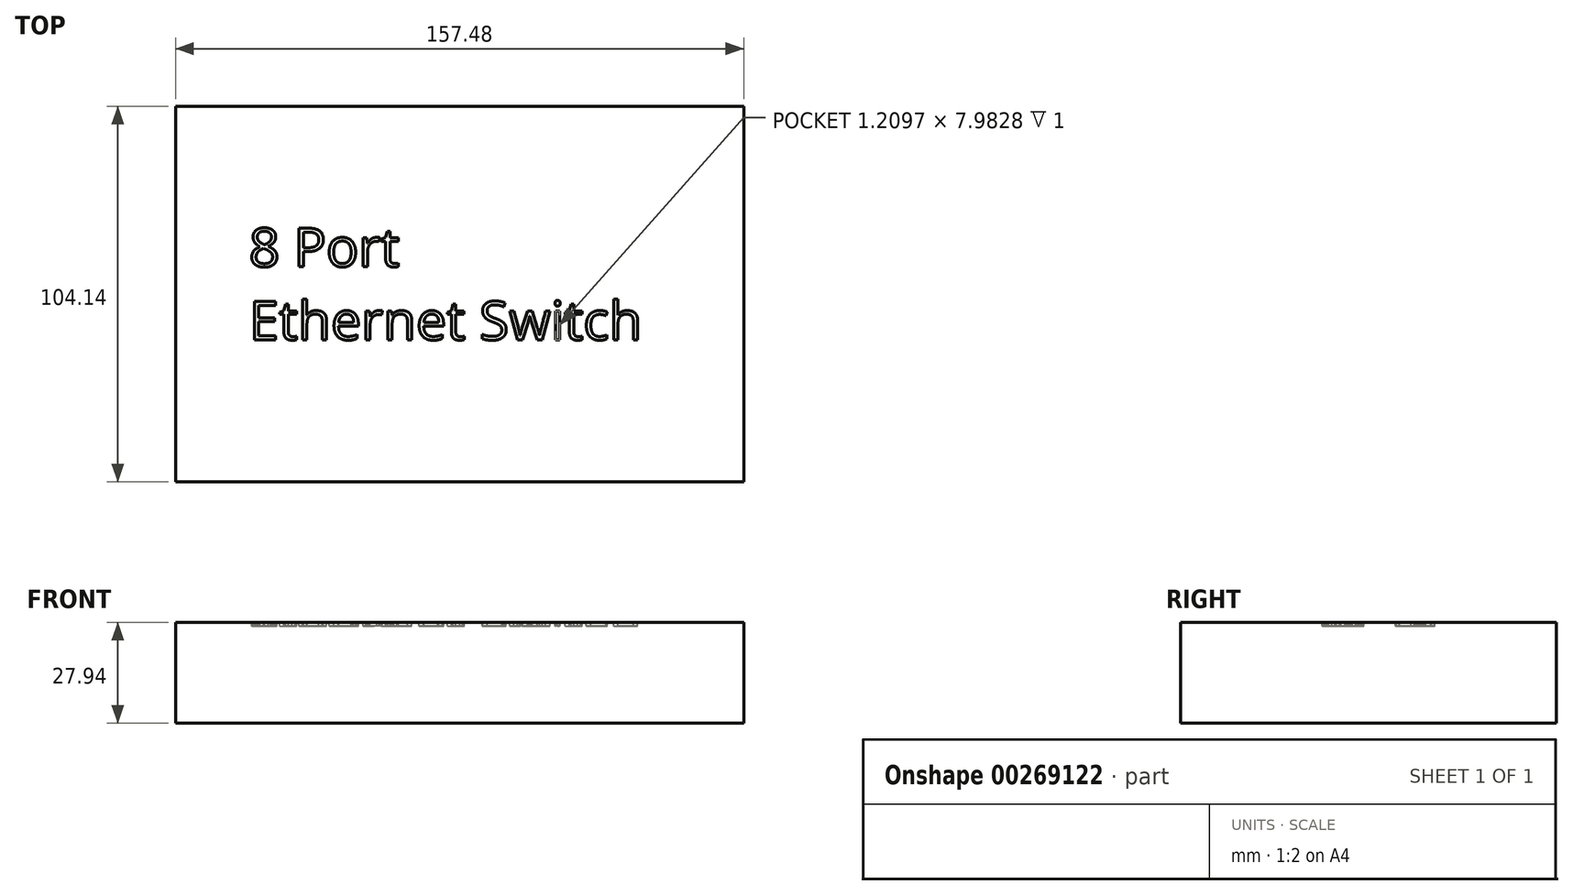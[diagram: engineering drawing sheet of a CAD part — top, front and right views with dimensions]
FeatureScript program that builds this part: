
annotation { "Feature Type Name" : "Feature", "Feature Type Description" : "" }
export const myFeature = defineFeature(function(context is Context, id is Id, definition is map)
    precondition{}
    {
        {
            var Q0;
            Q0=qCreatedBy(makeId("Top.planeOp"),FACE);
            var sketch = newSketch(context, id + "F0", { "sketchPlane" : qUnion([Q0])});
            skLineSegment(sketch, "E0.bottom", {"start": v(78.74, 52.07) * mm, "end": v(-78.74, 52.07) * mm});
            skLineSegment(sketch, "E0.top", {"start": v(78.74, -52.07) * mm, "end": v(-78.74, -52.07) * mm});
            skLineSegment(sketch, "E0.left", {"start": v(78.74, 52.07) * mm, "end": v(78.74, -52.07) * mm});
            skLineSegment(sketch, "E0.right", {"start": v(-78.74, 52.07) * mm, "end": v(-78.74, -52.07) * mm});
            skPoint(sketch, "E0.middle", {"position": v(0, 0) * mm});
            skSolve(sketch);
        }
        {
            var Q0;
            Q0 = qSketchRegion(id + "F0", true);
            extrude(context, id + "F1", {"entities" : qUnion([Q0]), "depth" : 27.94 * mm});
        }
        {
            var Q0;
            Q0=makeQuery(id+"F1.opExtrude","CAP_FACE",FACE,{"disambiguationData":[OSD([sQuery(id+"F0.wireOp",EDGE,"E0.bottom"),sQuery(id+"F0.wireOp",EDGE,"E0.top"),sQuery(id+"F0.wireOp",EDGE,"E0.left"),sQuery(id+"F0.wireOp",EDGE,"E0.right")])],"isStart":false});
            var sketch = newSketch(context, id + "F2", { "sketchPlane" : qUnion([Q0])});
            skText(sketch, "E1", { "text": "8 Port \nEthernet Switch", "fontName": "OpenSans-Regular.ttf"});
            const initialGuessF2  = {"E1": [-0.05837, 0.0076, 1, 0, 0.01074]};
            skSetInitialGuess(sketch, initialGuessF2);
            skSolve(sketch);
        }
        {
            var Q0;
            Q0 = qSketchRegion(id + "F2", true);
            extrude(context, id + "F3", {"entities" : qUnion([Q0]), "operationType" : NewBodyOperationType.REMOVE, "oppositeDirection" : true, "depth" : 1 * mm});
        }
    });
